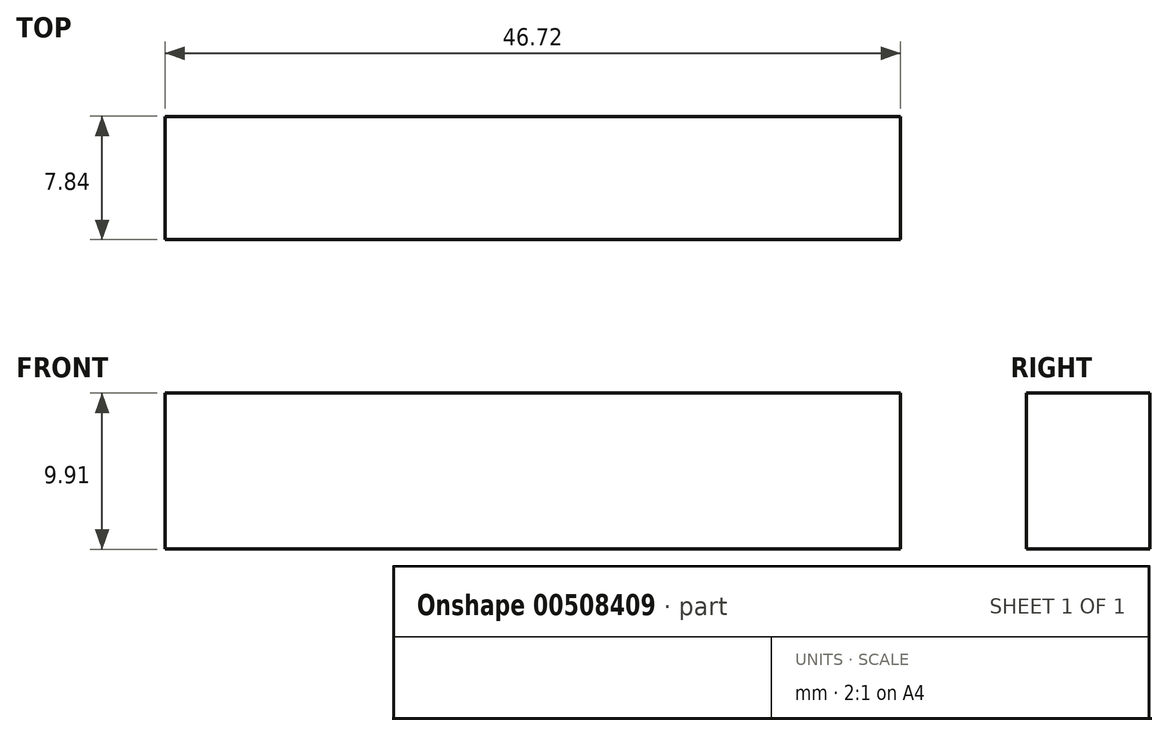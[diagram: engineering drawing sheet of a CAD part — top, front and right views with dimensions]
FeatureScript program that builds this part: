
annotation { "Feature Type Name" : "Feature", "Feature Type Description" : "" }
export const myFeature = defineFeature(function(context is Context, id is Id, definition is map)
    precondition{}
    {
        {
            var Q0;
            Q0=qCreatedBy(makeId("Top.planeOp"),FACE);
            var sketch = newSketch(context, id + "F0", { "sketchPlane" : qUnion([Q0])});
            skLineSegment(sketch, "E0.bottom", {"start": v(-23.36, -3.92) * mm, "end": v(23.36, -3.92) * mm});
            skLineSegment(sketch, "E0.top", {"start": v(-23.36, 3.92) * mm, "end": v(23.36, 3.92) * mm});
            skLineSegment(sketch, "E0.left", {"start": v(-23.36, -3.92) * mm, "end": v(-23.36, 3.92) * mm});
            skLineSegment(sketch, "E0.right", {"start": v(23.36, -3.92) * mm, "end": v(23.36, 3.92) * mm});
            skPoint(sketch, "E0.middle", {"position": v(0, 0) * mm});
            skSolve(sketch);
        }
        {
            var Q0;
            Q0=makeQuery(id+"F0.imprint","IMPRINT",FACE,{"disambiguationData":[TD([[makeQuery(id+"F0.imprint","IMPRINT",EDGE,{"derivedFrom":sQuery(id+"F0.wireOp",EDGE,"E0.bottom")}),1.0]])]});
            var sketch = newSketch(context, id + "F1", { "sketchPlane" : qUnion([Q0])});
            skCircle(sketch, "E1", {"center": v(-19.47, 0) * mm, "radius": 2.41 * mm});
            skSolve(sketch);
        }
        {
            var Q0;
            Q0=makeQuery(id+"F0.imprint","IMPRINT",FACE,{"disambiguationData":[TD([[makeQuery(id+"F0.imprint","IMPRINT",EDGE,{"derivedFrom":sQuery(id+"F0.wireOp",EDGE,"E0.bottom")}),1.0]])]});
            var sketch = newSketch(context, id + "F2", { "sketchPlane" : qUnion([Q0])});
            skCircle(sketch, "E2", {"center": v(-11.68, 0) * mm, "radius": 2.41 * mm});
            skSolve(sketch);
        }
        {
            var Q0;
            Q0=makeQuery(id+"F0.imprint","IMPRINT",FACE,{"disambiguationData":[TD([[makeQuery(id+"F0.imprint","IMPRINT",EDGE,{"derivedFrom":sQuery(id+"F0.wireOp",EDGE,"E0.bottom")}),1.0]])]});
            var sketch = newSketch(context, id + "F3", { "sketchPlane" : qUnion([Q0])});
            skCircle(sketch, "E3", {"center": v(-3.9, 0) * mm, "radius": 2.41 * mm});
            skSolve(sketch);
        }
        {
            var Q0;
            Q0=makeQuery(id+"F0.imprint","IMPRINT",FACE,{"disambiguationData":[TD([[makeQuery(id+"F0.imprint","IMPRINT",EDGE,{"derivedFrom":sQuery(id+"F0.wireOp",EDGE,"E0.bottom")}),1.0]])]});
            var sketch = newSketch(context, id + "F4", { "sketchPlane" : qUnion([Q0])});
            skCircle(sketch, "E4", {"center": v(3.9, 0) * mm, "radius": 2.41 * mm});
            skSolve(sketch);
        }
        {
            var Q0;
            Q0 = qSketchRegion(id + "F0", true);
            extrude(context, id + "F5", {"entities" : qUnion([Q0]), "oppositeDirection" : true, "depth" : 9.9 * mm});
        }
    });
